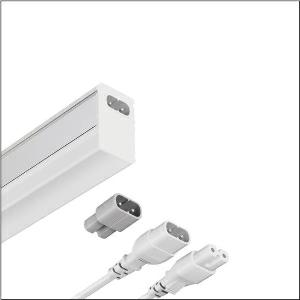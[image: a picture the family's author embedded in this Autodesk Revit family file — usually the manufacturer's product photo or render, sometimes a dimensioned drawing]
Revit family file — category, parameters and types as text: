
# Revit family: batten_41-e_51lp327km20ae
name_source: partatom
category: Lighting Fixtures
units: mm (PartAtom-declared; Revit-internal decimal feet)

## family parameters
Cut with Voids When Loaded = No
Host = Face
Light Source = No
Part Type = Normal
Room Calculation Point = No
Round Connector Dimension = Use Diameter
Shared = No

## types (1)
- --- (1 x LED, 2000 lm, 16 W, 5000K)
    Apparent Load = 16 VA
    CIE Flux Codes = 37 66 87 87 100
    Color Rendering = 80
    Color Temperature = 5000K
    Default Elevation = 1800 mm
    Description = Batten 41-E, batten luminaire, primary optical cover: cover, of PC, frosted, light emission: direct distribution, primary light characteristic: symmetric, installation type: surface-mounted, LED, rated luminous flux: 2.000lm, luminous efficacy: 125lm/W, light colour: 830/840/850, colour temperature: 3000/4000/5000K, control gear: ECG, with system connector: socket, mains connection: 220..240V, AC, 50/60Hz, rated input power: 16W, housing, of aluminium, silver, length: 1.180mm, width: 25mm, height: 44mm, end cap, of PC, white, protection rating (complete): IP20, insulation class (complete): insulation class II (safety insulation), certification: CE, permissible operating ambient temperature: -20..+40°C, packaging unit: 1 piece
    Height = 44 mm
    Lamp = 1 x LED
    Lamp Light Flux = 2000 lm
    Lamp Power = 16 W
    Lamp count = 1
    Length = 1180 mm
    Luminous efficacy = 125 lm/W
    Manufacturer = Siteco
    ModVariant = No
    Model = 51LP327KM20AE
    Mounting Place = Ceiling
    Mounting Type = Surface mounted
    Number of Poles = 1
    OnlyDefault = Yes
    Power Factor = 1
    Product Name = Batten 41-E
    Product group = batten luminaire
    ProductGroupID = 301
    Protection Class = Protection class II
    Protection Degree = IP 20
    RLX_Detail_Level = 1
    RLX_Emergency_Light_Flux = 0 lm
    RLX_Emergency_Type = 0
    RLX_Emergency_Type_DB = No
    RlxData = <blob elided: 37277 chars, md5=d6cfd83c>
    Socket = socket
    Standby Power = 0 W
    System Light Flux = 2000 lm
    System Power = 16 W
    Type Comments = individual setting: colour temperature 5000K
    Type Image = l_1007257.jpg
    URL = http://relux.com
    VarID = @adj_000295
    Voltage = 0 V
    Weight = 0.00 kg
    Width = 25 mm  [stored 0.082021 ft]

note: [stored X ft] marks values corroborated as IEEE doubles in the binary element streams (Revit-internal decimal feet)

## geometry (parser evidence)
native form markers: Blend x4, Sweep x13
no freeform markers — native parametric forms only
